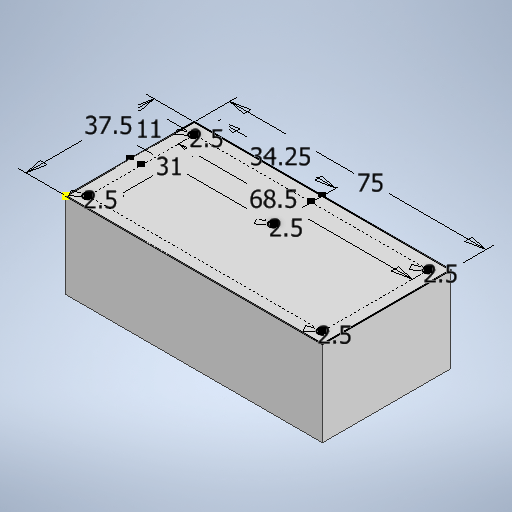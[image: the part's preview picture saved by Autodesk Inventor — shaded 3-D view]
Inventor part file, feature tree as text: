
AUTODESK INVENTOR PART (.ipt)
format: ipt  version: 2025.2 (Build 292293000, 293)  size: 231,936 bytes
history: native  units: in
note: dims shown in document units (in); Inventor stores cm internally (conversion verified against a paired STEP export)
features: extrude x2, sketch x1
ambient origin geometry x8: Origin, YZ Plane, XZ Plane, XY Plane, X Axis, Y Axis, Z Axis, Center Point
bodies: Solid1 (feature_tree)
feature tree (3):
  sketch  "Sketch1"  dims[d0=1.4764in d1=2.9528in d2=1.2205in d3=2.6969in d4=0.0984in d6=0.0984in d7=0.0984in d8=0.0984in d9=0.0984in d10=1.3484in d11=0.4331in d12=0.9843in d13=0.0in d14=0.315in d15=0.0in]
  extrude  "Extrusion1"  Depth=2.9528in
  extrude  "Extrusion2"  Depth=0.315in
